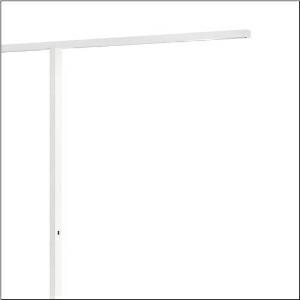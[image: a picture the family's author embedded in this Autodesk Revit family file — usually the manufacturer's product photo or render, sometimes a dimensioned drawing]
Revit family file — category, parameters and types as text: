
# Revit family: silica_r__11_floor_duo_5mx51bs8wzk00006xx_4f95
name_source: partatom
category: Lighting Fixtures
units: mm (PartAtom-declared; Revit-internal decimal feet)

## family parameters
Cut with Voids When Loaded = No
Host = Face
Light Source = No
Part Type = Normal
Room Calculation Point = No
Round Connector Dimension = Use Diameter
Shared = No

## types (1)
- --- (1 x LED, 3970 lm / 8500 lm, 24.1 W / 53.2 W, 4000K)
    Apparent Load = 155 VA
    CIE Flux Codes = 82 97 100 100 100 / - - - 0 100
    Color Rendering = 80
    Color Temperature = 4000K
    Default Elevation = 1800 mm
    Description = Silica® 11 Floor duo, floorstanding luminaire, of PMMA, primary optical cover: cover panel, of PMMA, light emission: indirect/direct distribution, primary light characteristic: symmetric, installation type: not mounted, LED, rated luminous flux: 24.930lm, luminous efficacy: 161lm/W, light colour: 840, colour temperature: 4000K, control gear: DALI, daylight-dependent control, mains connection: 230V, AC, 50Hz, connection cable pre-assembled, cable length: 3m, rated input power: 155W, luminaire head, rectangular, rounded, of aluminium, coated, traffic white (RAL 9016), supporting column, angular, of aluminium, coated, traffic white (RAL 9016), baseplate, of steel, coated, traffic white (RAL 9016), length: 2.598mm, width: 65mm, protection rating (complete): IP20, insulation class (complete): insulation class I (protective earthing), certification: CE, permissible operating ambient temperature: 0..+35°C, standard: EN 50419, packaging unit: 1 piece
    Height = 40 mm  [stored 0.131234 ft]
    Lamp = 1 x LED
    Lamp Light Flux = 3970 lm / 8500 lm
    Lamp Power = 24.1 W / 53.2 W
    Lamp count = 1
    Length = 2598 mm
    Luminous efficacy = 161 lm/W
    Manufacturer = Siteco
    ModVariant = No
    Model = 5MX51BS8WZK00006XX
    Mounting Place = Floor
    Mounting Type = Freestanding
    Number of Poles = 1
    OnlyDefault = Yes
    Power Factor = 1
    Product Name = Silica® 11 Floor duo
    Product group = floorstanding luminaire
    ProductGroupID = 1302
    Protection Class = Protection class I
    Protection Degree = IP 20
    RLX_Detail_Level = 1
    RLX_Emergency_Light_Flux = 0 lm
    RLX_Emergency_Type = 0
    RLX_Emergency_Type_DB = No
    RlxData = <blob elided: 19221 chars, md5=100282ac>
    Socket = socket
    Standby Power = 0 W
    System Light Flux = 24940 lm
    System Power = 155 W
    Type Comments = factory setting: direct and indirect light
    Type Image = l_1004652.jpg
    URL = http://relux.com
    VarID = @adj_199216
    Voltage = 0 V
    Weight = 0.00 kg
    Width = 65 mm

note: [stored X ft] marks values corroborated as IEEE doubles in the binary element streams (Revit-internal decimal feet)

## geometry (parser evidence)
native form markers: Blend x4, Sweep x19
no freeform markers — native parametric forms only
